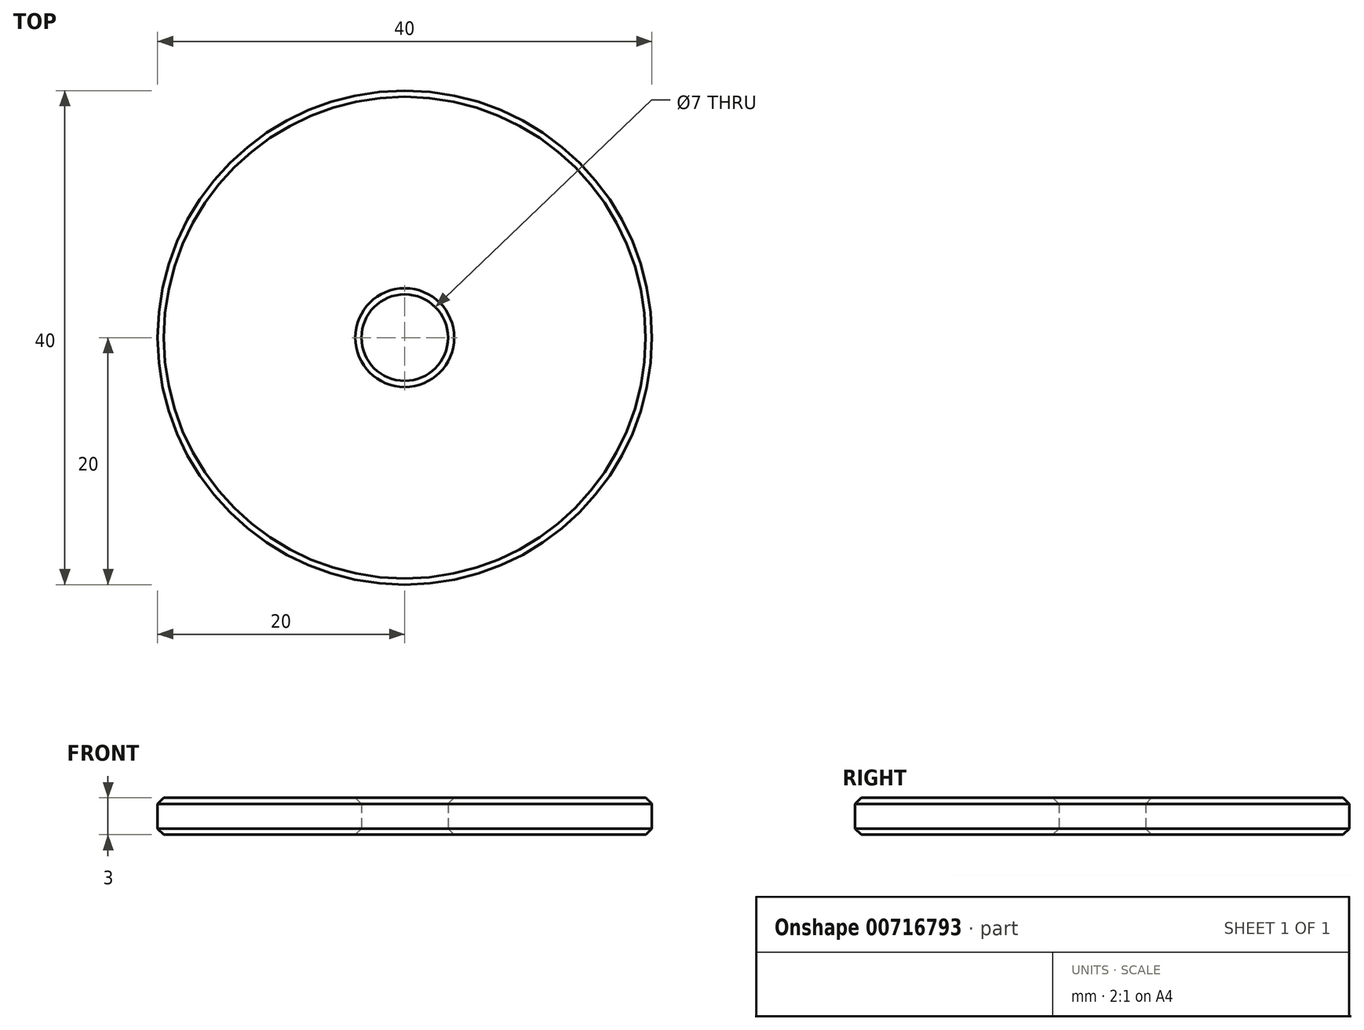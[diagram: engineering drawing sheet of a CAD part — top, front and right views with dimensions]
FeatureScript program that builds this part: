
annotation { "Feature Type Name" : "Feature", "Feature Type Description" : "" }
export const myFeature = defineFeature(function(context is Context, id is Id, definition is map)
    precondition{}
    {
        {
            var Q0;
            Q0=qCreatedBy(makeId("Top.planeOp"),FACE);
            var sketch = newSketch(context, id + "F0", { "sketchPlane" : qUnion([Q0])});
            skCircle(sketch, "E0", {"center": v(0, 0) * mm, "radius": 20 * mm});
            skCircle(sketch, "E1", {"center": v(0, 0) * mm, "radius": 3.5 * mm});
            skSolve(sketch);
        }
        {
            var Q0;
            Q0 = qSketchRegion(id + "F0", true);
            extrude(context, id + "F1", {"entities" : qUnion([Q0]), "endBound" : BoundingType.SYMMETRIC, "depth" : 3 * mm, "offsetDistance" : 25 * mm});
        }
        {
            var Q0;
            Q0=makeQuery(id+"F1.opExtrude","CAP_FACE",FACE,{"disambiguationData":[OSD([sQuery(id+"F0.wireOp",EDGE,"E0"),sQuery(id+"F0.wireOp",EDGE,"E1")])],"isStart":false});
            var Q1;
            Q1=makeQuery(id+"F1.opExtrude","CAP_FACE",FACE,{"disambiguationData":[OSD([sQuery(id+"F0.wireOp",EDGE,"E0"),sQuery(id+"F0.wireOp",EDGE,"E1")])],"isStart":true});
            chamfer(context, id + "F2", {"entities" : qUnion([Q0, Q1]), "width" : 0.5 * mm, "tangentPropagation" : true});
        }
    });
